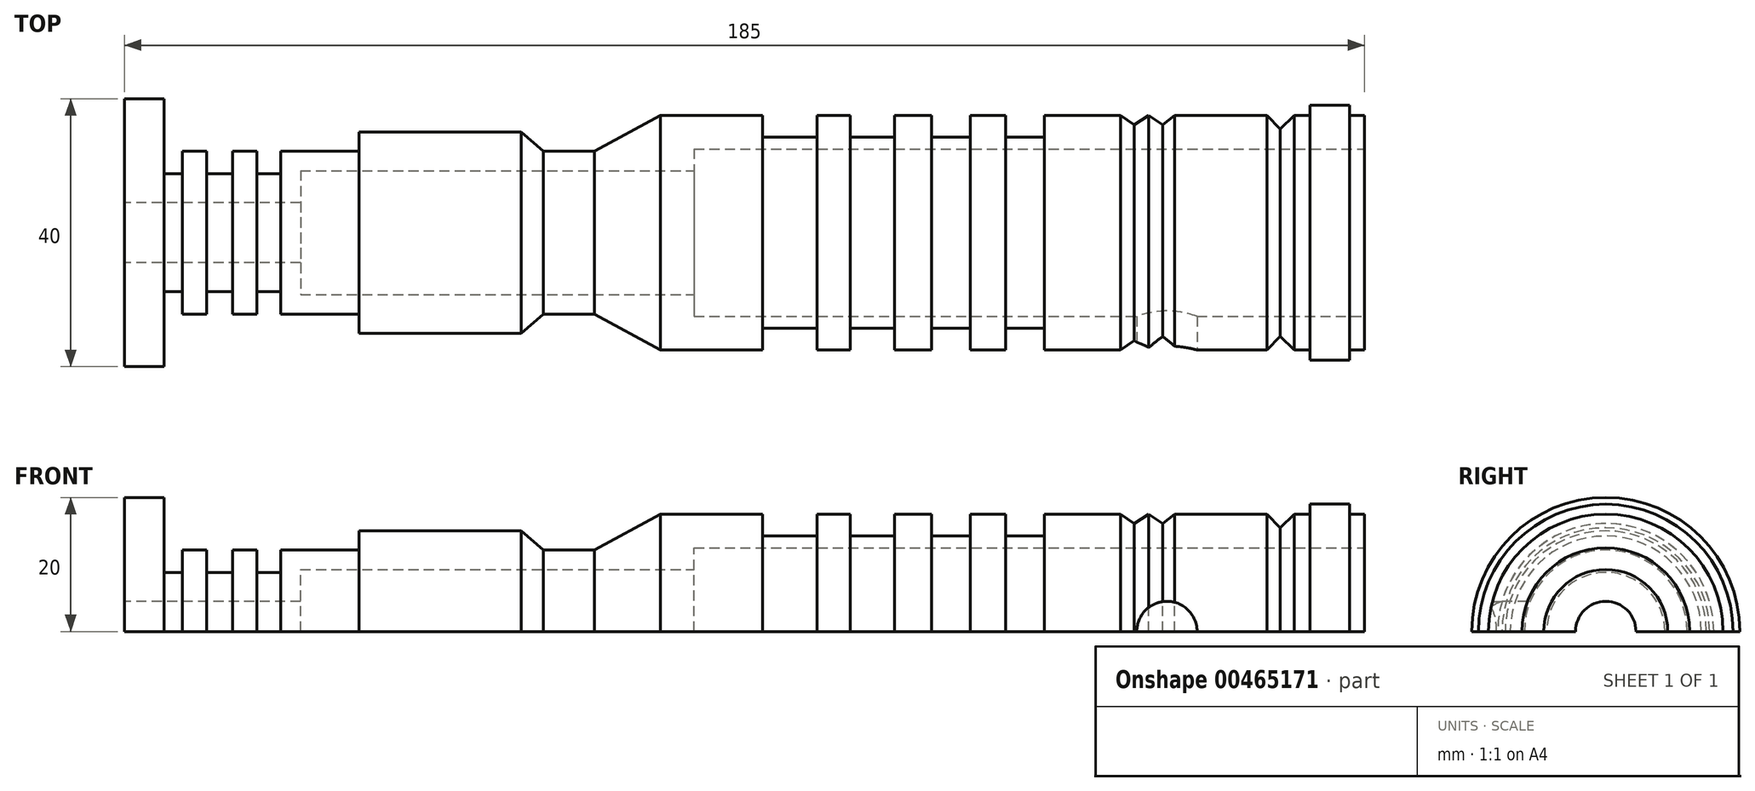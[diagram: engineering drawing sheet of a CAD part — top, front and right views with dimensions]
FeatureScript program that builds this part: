
annotation { "Feature Type Name" : "Feature", "Feature Type Description" : "" }
export const myFeature = defineFeature(function(context is Context, id is Id, definition is map)
    precondition{}
    {
        {
            var Q0;
            Q0=qCreatedBy(makeId("Top.planeOp"),FACE);
            var sketch = newSketch(context, id + "F0", { "sketchPlane" : qUnion([Q0])});
            skLineSegment(sketch, "E0", {"start": v(-125.78, 5) * mm, "end": v(-150, 5) * mm});
            skLineSegment(sketch, "E1", {"start": v(-179.09, 0) * mm, "end": v(-185, 0) * mm});
            skLineSegment(sketch, "E2", {"start": v(-185, 0) * mm, "end": v(-185, 20) * mm});
            skLineSegment(sketch, "E3", {"start": v(-185, 20) * mm, "end": v(0, 20) * mm});
            skLineSegment(sketch, "E4", {"start": v(0, 20) * mm, "end": v(0, 2.5) * mm});
            skLineSegment(sketch, "E5", {"start": v(-179.09, 0) * mm, "end": v(-179.09, 11.18) * mm});
            skLineSegment(sketch, "E6", {"start": v(-179.09, 11.18) * mm, "end": v(-176.32, 11.18) * mm});
            skLineSegment(sketch, "E7", {"start": v(-176.32, 11.18) * mm, "end": v(-176.32, 7.86) * mm});
            skLineSegment(sketch, "E8", {"start": v(-176.32, 7.86) * mm, "end": v(-172.72, 7.86) * mm});
            skLineSegment(sketch, "E9", {"start": v(-172.72, 7.86) * mm, "end": v(-172.72, 11.18) * mm});
            skLineSegment(sketch, "E10", {"start": v(-172.72, 11.18) * mm, "end": v(-168.85, 11.18) * mm});
            skLineSegment(sketch, "E11", {"start": v(-168.85, 11.18) * mm, "end": v(-168.85, 7.86) * mm});
            skLineSegment(sketch, "E12", {"start": v(-168.85, 7.86) * mm, "end": v(-165.25, 7.86) * mm});
            skLineSegment(sketch, "E13", {"start": v(-165.25, 7.86) * mm, "end": v(-165.25, 11.18) * mm});
            skLineSegment(sketch, "E14", {"start": v(-165.25, 11.18) * mm, "end": v(-161.65, 11.18) * mm});
            skLineSegment(sketch, "E15", {"start": v(-161.65, 11.18) * mm, "end": v(-161.65, 7.86) * mm});
            skLineSegment(sketch, "E16", {"start": v(-161.65, 7.86) * mm, "end": v(-150, 7.86) * mm});
            skLineSegment(sketch, "E17", {"start": v(-150, 7.86) * mm, "end": v(-150, 5) * mm});
            skPoint(sketch, "E18.end.orphan", {"position": v(-160, 0) * mm});
            skLineSegment(sketch, "E19", {"start": v(-125.78, 5) * mm, "end": v(-122.5, 7.86) * mm});
            skLineSegment(sketch, "E20", {"start": v(-122.5, 7.86) * mm, "end": v(-114.84, 7.86) * mm});
            skLineSegment(sketch, "E21", {"start": v(-105, 2.5) * mm, "end": v(-89.8, 2.5) * mm});
            skLineSegment(sketch, "E22", {"start": v(-89.8, 2.5) * mm, "end": v(-89.8, 5.75) * mm});
            skLineSegment(sketch, "E23", {"start": v(-89.8, 5.75) * mm, "end": v(-81.66, 5.75) * mm});
            skLineSegment(sketch, "E24", {"start": v(-81.66, 5.75) * mm, "end": v(-81.66, 2.5) * mm});
            skLineSegment(sketch, "E25", {"start": v(-81.66, 2.5) * mm, "end": v(-76.67, 2.5) * mm});
            skLineSegment(sketch, "E26", {"start": v(-76.67, 2.5) * mm, "end": v(-76.67, 5.75) * mm});
            skLineSegment(sketch, "E27", {"start": v(-76.67, 5.75) * mm, "end": v(-70.1, 5.75) * mm});
            skLineSegment(sketch, "E28", {"start": v(-70.1, 5.75) * mm, "end": v(-70.1, 2.5) * mm});
            skLineSegment(sketch, "E29", {"start": v(-70.1, 2.5) * mm, "end": v(-64.59, 2.5) * mm});
            skLineSegment(sketch, "E30", {"start": v(-64.59, 2.5) * mm, "end": v(-64.59, 5.75) * mm});
            skLineSegment(sketch, "E31", {"start": v(-64.59, 5.75) * mm, "end": v(-58.8, 5.75) * mm});
            skLineSegment(sketch, "E32", {"start": v(-58.8, 5.75) * mm, "end": v(-58.8, 2.5) * mm});
            skLineSegment(sketch, "E33", {"start": v(-58.8, 2.5) * mm, "end": v(-53.55, 2.5) * mm});
            skLineSegment(sketch, "E34", {"start": v(-53.55, 2.5) * mm, "end": v(-53.55, 5.75) * mm});
            skLineSegment(sketch, "E35", {"start": v(-53.55, 5.75) * mm, "end": v(-47.77, 5.75) * mm});
            skLineSegment(sketch, "E36", {"start": v(-47.77, 5.75) * mm, "end": v(-47.77, 2.5) * mm});
            skLineSegment(sketch, "E37", {"start": v(-47.77, 2.5) * mm, "end": v(-36.38, 2.5) * mm});
            skLineSegment(sketch, "E38", {"start": v(-10.48, 2.5) * mm, "end": v(-8.13, 2.5) * mm});
            skPoint(sketch, "E39.orphan", {"position": v(0, 0) * mm});
            skPoint(sketch, "E40.orphan", {"position": v(-100, 0) * mm});
            skPoint(sketch, "E41.end.orphan", {"position": v(-110, 5) * mm});
            skLineSegment(sketch, "E42", {"start": v(-114.84, 7.86) * mm, "end": v(-105, 2.5) * mm});
            skLineSegment(sketch, "E43", {"start": v(-14.53, 2.5) * mm, "end": v(-12.57, 4.52) * mm});
            skLineSegment(sketch, "E44", {"start": v(-12.57, 4.52) * mm, "end": v(-10.48, 2.5) * mm});
            skLineSegment(sketch, "E45", {"start": v(-8.13, 2.5) * mm, "end": v(-8.13, 1.01) * mm});
            skLineSegment(sketch, "E46", {"start": v(-8.13, 1.01) * mm, "end": v(-2.23, 1.01) * mm});
            skLineSegment(sketch, "E47", {"start": v(-2.23, 1.01) * mm, "end": v(-2.23, 2.5) * mm});
            skPoint(sketch, "E48.orphan", {"position": v(-12.57, 2.5) * mm});
            skLineSegment(sketch, "E49.trimOffspring", {"start": v(-2.23, 2.5) * mm, "end": v(0, 2.5) * mm});
            skLineSegment(sketch, "E50", {"start": v(-28.32, 2.5) * mm, "end": v(-30.11, 3.89) * mm});
            skLineSegment(sketch, "E51", {"start": v(-30.11, 3.89) * mm, "end": v(-32.16, 2.5) * mm});
            skLineSegment(sketch, "E52", {"start": v(-32.16, 2.5) * mm, "end": v(-34.34, 3.89) * mm});
            skLineSegment(sketch, "E53", {"start": v(-34.34, 3.89) * mm, "end": v(-36.38, 2.5) * mm});
            skLineSegment(sketch, "E54.trimOffspring", {"start": v(-28.32, 2.5) * mm, "end": v(-14.53, 2.5) * mm});
            skSolve(sketch);
        }
        {
            var Q0;
            Q0=makeQuery(id+"F0.imprint","IMPRINT",FACE,{"disambiguationData":[TD([[makeQuery(id+"F0.imprint","IMPRINT",EDGE,{"derivedFrom":sQuery(id+"F0.wireOp",EDGE,"E0")}),-1.0]])]});
            var Q1;
            Q1=sQuery(id+"F0.wireOp",EDGE,"E3");
            revolve(context, id + "F1", {"entities" : qUnion([Q0]), "axis" : qUnion([Q1]), "revolveType" : RevolveType.ONE_DIRECTION, "oppositeDirection" : true, "angle" : 180 * degree});
        }
        {
            var Q0;
            Q0=makeQuery(id+"F1.opRevolve","SWEPT_FACE",FACE,{"disambiguationData":[OSD([sQuery(id+"F0.wireOp",EDGE,"E2")])]});
            var sketch = newSketch(context, id + "F2", { "sketchPlane" : qUnion([Q0])});
            skCircle(sketch, "E55", {"center": v(-20, 0) * mm, "radius": 4.5 * mm});
            skSolve(sketch);
        }
        {
            var Q0;
            Q0=makeQuery(id+"F2.imprint","IMPRINT",FACE,{"disambiguationData":[TD([[makeQuery(id+"F2.imprint","IMPRINT",EDGE,{"derivedFrom":sQuery(id+"F2.wireOp",EDGE,"E55")}),1.0]])]});
            extrude(context, id + "F3", {"entities" : qUnion([Q0]), "operationType" : NewBodyOperationType.REMOVE, "oppositeDirection" : true, "depth" : 127.6 * mm});
        }
        {
            var Q0;
            Q0=makeQuery(id+"F1.opRevolve","SWEPT_FACE",FACE,{"disambiguationData":[OSD([sQuery(id+"F0.wireOp",EDGE,"E4")])]});
            var sketch = newSketch(context, id + "F4", { "sketchPlane" : qUnion([Q0])});
            skCircle(sketch, "E56", {"center": v(20, 0) * mm, "radius": 12.5 * mm});
            skSolve(sketch);
        }
        {
            var Q0;
            Q0=makeQuery(id+"F4.imprint","IMPRINT",FACE,{"disambiguationData":[TD([[makeQuery(id+"F4.imprint","IMPRINT",EDGE,{"derivedFrom":sQuery(id+"F4.wireOp",EDGE,"E56")}),1.0]])]});
            extrude(context, id + "F5", {"entities" : qUnion([Q0]), "operationType" : NewBodyOperationType.REMOVE, "oppositeDirection" : true, "depth" : 100 * mm});
        }
        {
            var Q0;
            Q0=qCreatedBy(makeId("Front.planeOp"),FACE);
            var sketch = newSketch(context, id + "F6", { "sketchPlane" : qUnion([Q0])});
            skCircle(sketch, "E57", {"center": v(-29.46, 0) * mm, "radius": 4.5 * mm});
            skSolve(sketch);
        }
        {
            var Q0;
            Q0=makeQuery(id+"F6.imprint","IMPRINT",FACE,{"disambiguationData":[TD([[makeQuery(id+"F6.imprint","IMPRINT",EDGE,{"derivedFrom":sQuery(id+"F6.wireOp",EDGE,"E57")}),1.0]])]});
            extrude(context, id + "F7", {"entities" : qUnion([Q0]), "operationType" : NewBodyOperationType.REMOVE, "oppositeDirection" : true, "depth" : 16.8 * mm});
        }
        {
            var Q0;
            Q0=makeQuery(id+"F5.boolean.opBoolean","COPY",FACE,{"derivedFrom":makeQuery(id+"F5.opExtrude","CAP_FACE",FACE,{"disambiguationData":[OSD([sQuery(id+"F4.wireOp",EDGE,"E56")])],"isStart":false})});
            var sketch = newSketch(context, id + "F8", { "sketchPlane" : qUnion([Q0])});
            skCircle(sketch, "E58", {"center": v(20, 0) * mm, "radius": 9.25 * mm});
            skSolve(sketch);
        }
        {
            var Q0;
            {var subQ1=makeQuery(id+"F5.opExtrude","CAP_FACE",FACE,{"disambiguationData":[OSD([sQuery(id+"F4.wireOp",EDGE,"E56")])],"isStart":false});var subQ7=makeQuery(id+"F5.boolean.opBoolean","INTERSECT",EDGE,{"derivedFrom":[makeQuery(id+"F3.boolean.opBoolean","COPY",FACE,{"derivedFrom":makeQuery(id+"F3.opExtrude","SWEPT_FACE",FACE,{"disambiguationData":[OSD([sQuery(id+"F2.wireOp",EDGE,"E55")])]})}),subQ1]});Q0=makeQuery(id+"F8.imprint","IMPRINT",FACE,{"disambiguationData":[TD([[makeQuery(id+"F8.imprint","IMPRINT",EDGE,{"derivedFrom":subQ7}),-1.0]])]});}
            var Q1;
            {var subQ1=makeQuery(id+"F5.opExtrude","CAP_FACE",FACE,{"disambiguationData":[OSD([sQuery(id+"F4.wireOp",EDGE,"E56")])],"isStart":false});var subQ7=makeQuery(id+"F5.boolean.opBoolean","INTERSECT",EDGE,{"derivedFrom":[makeQuery(id+"F3.boolean.opBoolean","COPY",FACE,{"derivedFrom":makeQuery(id+"F3.opExtrude","SWEPT_FACE",FACE,{"disambiguationData":[OSD([sQuery(id+"F2.wireOp",EDGE,"E55")])]})}),subQ1]});Q1=makeQuery(id+"F8.imprint","IMPRINT",FACE,{"disambiguationData":[TD([[makeQuery(id+"F8.imprint","IMPRINT",EDGE,{"derivedFrom":subQ7}),1.0]])]});}
            extrude(context, id + "F9", {"entities" : qUnion([Q0, Q1]), "operationType" : NewBodyOperationType.REMOVE, "oppositeDirection" : true, "depth" : 58.7 * mm});
        }
    });
